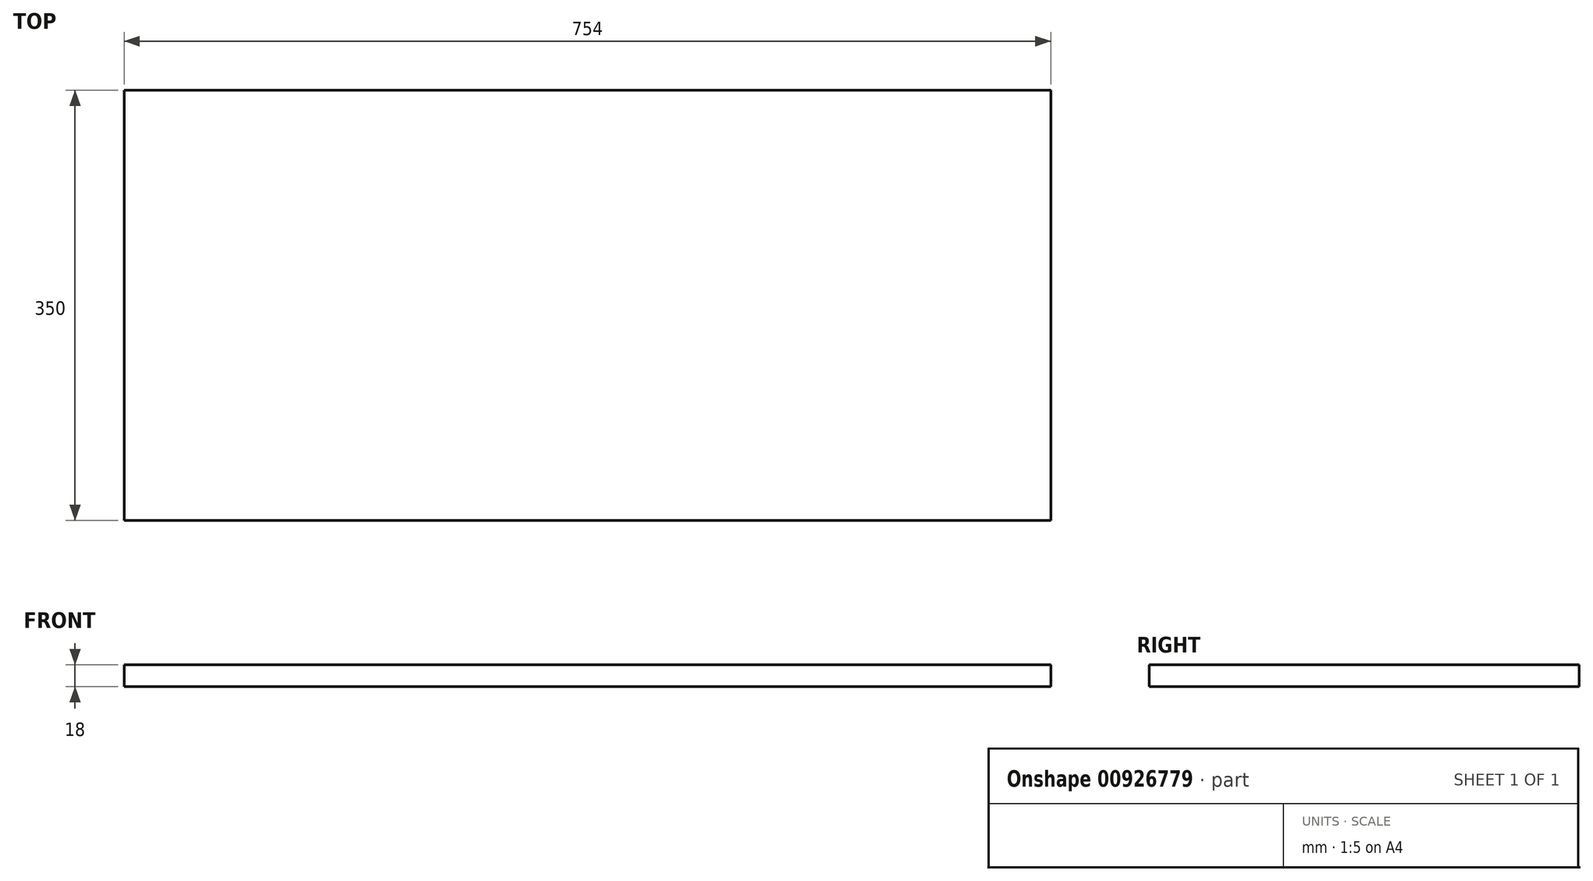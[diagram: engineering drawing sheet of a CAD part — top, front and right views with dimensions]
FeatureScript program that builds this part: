
annotation { "Feature Type Name" : "Feature", "Feature Type Description" : "" }
export const myFeature = defineFeature(function(context is Context, id is Id, definition is map)
    precondition{}
    {
        {
            var Q0;
            Q0=qCreatedBy(makeId("Top.planeOp"),FACE);
            var sketch = newSketch(context, id + "F0", { "sketchPlane" : qUnion([Q0])});
            skLineSegment(sketch, "E0.bottom", {"start": v(377, -175) * mm, "end": v(-377, -175) * mm});
            skLineSegment(sketch, "E0.top", {"start": v(377, 175) * mm, "end": v(-377, 175) * mm});
            skLineSegment(sketch, "E0.left", {"start": v(377, -175) * mm, "end": v(377, 175) * mm});
            skLineSegment(sketch, "E0.right", {"start": v(-377, -175) * mm, "end": v(-377, 175) * mm});
            skPoint(sketch, "E0.middle", {"position": v(0, 0) * mm});
            skSolve(sketch);
        }
        {
            var Q0;
            Q0 = qSketchRegion(id + "F0", true);
            extrude(context, id + "F1", {"entities" : qUnion([Q0]), "endBound" : BoundingType.SYMMETRIC, "depth" : 18 * mm, "offsetDistance" : 25 * mm});
        }
    });
